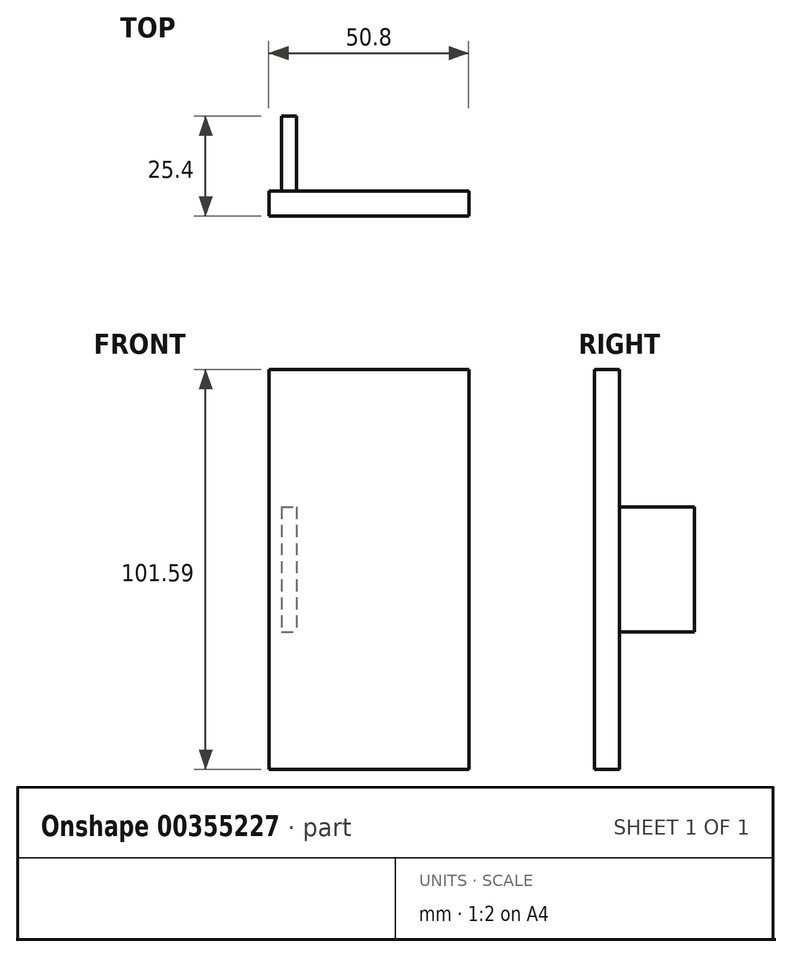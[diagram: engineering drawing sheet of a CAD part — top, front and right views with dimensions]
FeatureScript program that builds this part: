
annotation { "Feature Type Name" : "Feature", "Feature Type Description" : "" }
export const myFeature = defineFeature(function(context is Context, id is Id, definition is map)
    precondition{}
    {
        {
            var Q0;
            Q0=qCreatedBy(makeId("Top.planeOp"),FACE);
            var sketch = newSketch(context, id + "F0", { "sketchPlane" : qUnion([Q0])});
            skLineSegment(sketch, "E0.bottom", {"start": v(0, 0) * mm, "end": v(3.8, 0) * mm});
            skLineSegment(sketch, "E0.top", {"start": v(0, 19.05) * mm, "end": v(3.8, 19.05) * mm});
            skLineSegment(sketch, "E0.left", {"start": v(0, 0) * mm, "end": v(0, 19.05) * mm});
            skLineSegment(sketch, "E0.right", {"start": v(3.8, 0) * mm, "end": v(3.8, 19.05) * mm});
            skSolve(sketch);
        }
        {
            var Q0;
            Q0=makeQuery(id+"F0.imprint","IMPRINT",FACE,{"disambiguationData":[TD([[makeQuery(id+"F0.imprint","IMPRINT",EDGE,{"derivedFrom":sQuery(id+"F0.wireOp",EDGE,"E0.bottom")}),1.0]])]});
            extrude(context, id + "F1", {"entities" : qUnion([Q0]), "depth" : 31.75 * mm});
        }
        {
            var Q0;
            Q0=makeQuery(id+"F1.opExtrude","SWEPT_FACE",FACE,{"disambiguationData":[OSD([sQuery(id+"F0.wireOp",EDGE,"E0.bottom")])]});
            var sketch = newSketch(context, id + "F2", { "sketchPlane" : qUnion([Q0])});
            skLineSegment(sketch, "E1.bottom", {"start": v(-3.17, -34.93) * mm, "end": v(47.62, -34.93) * mm});
            skLineSegment(sketch, "E1.top", {"start": v(-3.18, 66.68) * mm, "end": v(47.62, 66.68) * mm});
            skLineSegment(sketch, "E1.left", {"start": v(-3.17, -34.93) * mm, "end": v(-3.18, 66.68) * mm});
            skLineSegment(sketch, "E1.right", {"start": v(47.63, -34.93) * mm, "end": v(47.62, 66.68) * mm});
            skSolve(sketch);
        }
        {
            var Q0;
            Q0=makeQuery(id+"F2.imprint","IMPRINT",FACE,{"disambiguationData":[TD([[makeQuery(id+"F2.imprint","IMPRINT",EDGE,{"derivedFrom":sQuery(id+"F2.wireOp",EDGE,"E1.bottom")}),1.0]])]});
            var Q1;
            {var subQ0=sQuery(id+"F0.wireOp",EDGE,"E0.bottom");Q1=makeQuery(id+"F2.imprint","IMPRINT",FACE,{"disambiguationData":[TD([[makeQuery(id+"F2.imprint","IMPRINT",EDGE,{"derivedFrom":makeQuery(id+"F1.opExtrude","CAP_EDGE",EDGE,{"disambiguationData":[OSD([subQ0])],"isStart":true})}),1.0]])]});}
            extrude(context, id + "F3", {"entities" : qUnion([Q0, Q1]), "operationType" : NewBodyOperationType.ADD, "depth" : 6.35 * mm, "offsetDistance" : 25.4 * mm});
        }
    });
